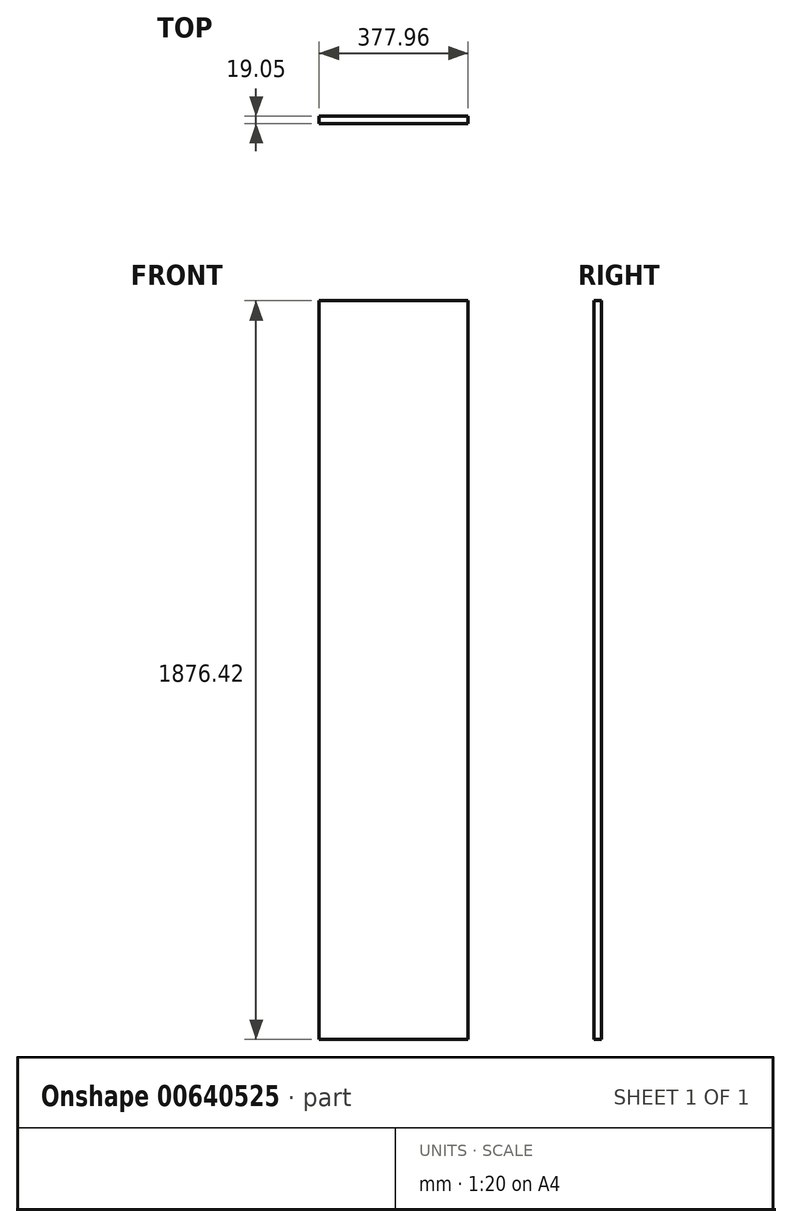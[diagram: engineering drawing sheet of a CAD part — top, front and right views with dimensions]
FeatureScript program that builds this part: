
annotation { "Feature Type Name" : "Feature", "Feature Type Description" : "" }
export const myFeature = defineFeature(function(context is Context, id is Id, definition is map)
    precondition{}
    {
        {
            var Q0;
            Q0=qCreatedBy(makeId("Front.planeOp"),FACE);
            var sketch = newSketch(context, id + "F0", { "sketchPlane" : qUnion([Q0])});
            skLineSegment(sketch, "E0.bottom", {"start": v(-188.98, 965.2) * mm, "end": v(188.98, 965.2) * mm});
            skLineSegment(sketch, "E0.top", {"start": v(-188.98, -965.2) * mm, "end": v(188.98, -965.2) * mm});
            skLineSegment(sketch, "E0.left", {"start": v(-188.98, 965.2) * mm, "end": v(-188.98, -965.2) * mm});
            skLineSegment(sketch, "E0.right", {"start": v(188.98, 965.2) * mm, "end": v(188.98, -965.2) * mm});
            skPoint(sketch, "E0.middle", {"position": v(0, 0) * mm});
            skSolve(sketch);
        }
        {
            var Q0;
            Q0=makeQuery(id+"F0.imprint","IMPRINT",FACE,{"disambiguationData":[TD([[makeQuery(id+"F0.imprint","IMPRINT",EDGE,{"derivedFrom":sQuery(id+"F0.wireOp",EDGE,"E0.bottom")}),-1.0]])]});
            extrude(context, id + "F1", {"entities" : qUnion([Q0]), "depth" : 19.05 * mm, "offsetDistance" : 25.4 * mm});
        }
        {
            var Q0;
            Q0=makeQuery(id+"F1.opExtrude","SWEPT_FACE",FACE,{"disambiguationData":[OSD([sQuery(id+"F0.wireOp",EDGE,"E0.top")])]});
            extrude(context, id + "F2", {"entities" : qUnion([Q0]), "operationType" : NewBodyOperationType.REMOVE, "oppositeDirection" : true, "depth" : 53.97 * mm, "offsetDistance" : 25.4 * mm});
        }
    });
